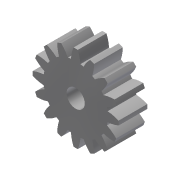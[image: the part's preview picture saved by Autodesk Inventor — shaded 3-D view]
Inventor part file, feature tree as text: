
AUTODESK INVENTOR PART (.ipt)
format: ipt  version: 2019.4 (Build 234330000, 330)  size: 227,840 bytes
history: native  units: mm (DEFAULTED — no unit token found)
features: other x5, plane x3, sketch x3, extrude x2, reference x2
ambient origin geometry x8: Origin, YZ Plane, XZ Plane, XY Plane, X Axis, Y Axis, Z Axis, Center Point
bodies: Solid1 (feature_tree)
feature tree (15):
  extrude  "Extrusion1"  Depth=6.0mm TaperAngle=0.0deg
  plane  "Work Plane2"
  plane  "Work Plane8"
  plane  "Work Plane9"
  other  "Spur Gear"
  extrude  "Extrusion2"  Depth=10.0mm TaperAngle=0.0deg
  sketch  "Sketch1"  dims[d0=18.0mm d1=6.0mm d2=0.0mm]
  sketch  "Sketch2"  dims[d3=16.0mm d4=10.0mm d5=0.0mm]
  other  "Srf1"
  reference  "Reference1"
  sketch  "Sketch3"  dims[d16=13.0mm d17=0.0mm d34=1.963495mm d39=0.0mm d41=0.0mm d43=13.0mm d46=13.0mm d47=0.0mm d48=0.0mm d49=3.8mm d50=0.3mm d51=3.0mm d52=-0.698132mm]
  reference  "Reference2"
  other  "Pitch Diameter"
  other  "Assembly_Opentrons_Autofocus_v2.iam"
  other  "DIN 912 - replaced by DIN EN ISO 4762 M4 x 20:1"
